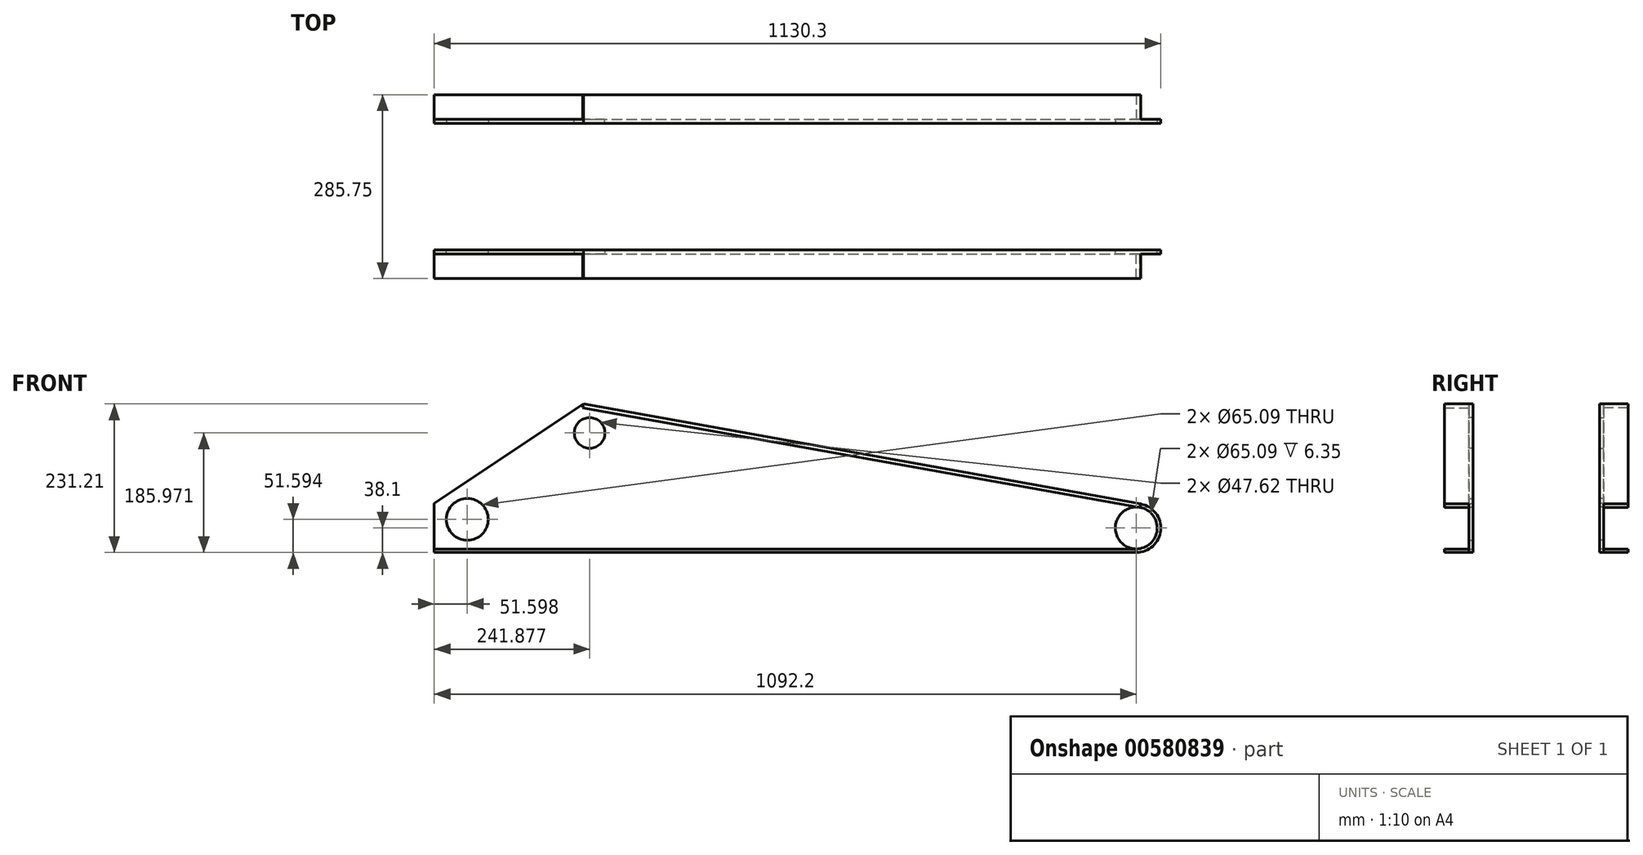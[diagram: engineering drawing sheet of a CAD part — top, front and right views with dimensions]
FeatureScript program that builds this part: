
annotation { "Feature Type Name" : "Feature", "Feature Type Description" : "" }
export const myFeature = defineFeature(function(context is Context, id is Id, definition is map)
    precondition{}
    {
        {
            var Q0;
            Q0=qCreatedBy(makeId("Front.planeOp"),FACE);
            var sketch = newSketch(context, id + "F0", { "sketchPlane" : qUnion([Q0])});
            skCircle(sketch, "E0", {"center": v(255.8, 0) * mm, "radius": 38.1 * mm});
            skLineSegment(sketch, "E1", {"start": v(-836.4, -38.1) * mm, "end": v(255.8, -38.1) * mm});
            skLineSegment(sketch, "E2", {"start": v(-836.4, -38.1) * mm, "end": v(-836.4, 38.1) * mm});
            skLineSegment(sketch, "E3", {"start": v(-836.4, 38.1) * mm, "end": v(-603.94, 193.11) * mm});
            skLineSegment(sketch, "E4", {"start": v(-603.94, 193.11) * mm, "end": v(262.54, 37.5) * mm});
            skCircle(sketch, "E5", {"center": v(-784.8, 13.5) * mm, "radius": 32.54 * mm});
            skCircle(sketch, "E6", {"center": v(255.8, 0) * mm, "radius": 32.54 * mm});
            skSolve(sketch);
        }
        {
            var Q0;
            {var subQ0=sQuery(id+"F0.wireOp",EDGE,"E1");Q0=makeQuery(id+"F0.imprint","IMPRINT",FACE,{"disambiguationData":[TD([[makeQuery(id+"F0.imprint","IMPRINT",EDGE,{"derivedFrom":subQ0}),1.0]])]});}
            var Q1;
            Q1=makeQuery(id+"F0.imprint","IMPRINT",FACE,{"disambiguationData":[TD([[makeQuery(id+"F0.imprint","IMPRINT",EDGE,{"derivedFrom":sQuery(id+"F0.wireOp",EDGE,"E6")}),-1.0]])]});
            var Q2;
            Q2=makeQuery(id+"F0.imprint","IMPRINT",FACE,{"disambiguationData":[TD([[makeQuery(id+"F0.imprint","IMPRINT",EDGE,{"derivedFrom":sQuery(id+"F0.wireOp",EDGE,"E2")}),-1.0]])]});
            var Q3;
            Q3=makeQuery(id+"F0.imprint","IMPRINT",FACE,{"disambiguationData":[TD([[makeQuery(id+"F0.imprint","IMPRINT",EDGE,{"derivedFrom":sQuery(id+"F0.wireOp",EDGE,"E4")}),1.0]])]});
            var Q4;
            Q4=makeQuery(id+"F0.imprint","IMPRINT",FACE,{"disambiguationData":[TD([[makeQuery(id+"F0.imprint","IMPRINT",EDGE,{"derivedFrom":sQuery(id+"F0.wireOp",EDGE,"E1")}),-1.0]])]});
            extrude(context, id + "F1", {"entities" : qUnion([Q0, Q1, Q2, Q3, Q4]), "depth" : 6.35 * mm, "offsetDistance" : 25.4 * mm});
        }
        {
            var Q0;
            {var subQ0=sQuery(id+"F0.wireOp",EDGE,"E2");var subQ1=sQuery(id+"F0.wireOp",EDGE,"E6");var subQ2=sQuery(id+"F0.wireOp",EDGE,"E5");var subQ3=sQuery(id+"F0.wireOp",EDGE,"E4");var subQ4=sQuery(id+"F0.wireOp",EDGE,"E3");var subQ5=makeQuery(id+"F1.opExtrude","CAP_FACE",FACE,{"disambiguationData":[OSD([sQuery(id+"F0.wireOp",EDGE,"E0"),sQuery(id+"F0.wireOp",EDGE,"E1"),subQ0,subQ4,subQ3,subQ2,subQ1])],"isStart":false});Q0=makeQuery(id+"FXa5xh8lsfBcW2b_1.boolean.opBoolean","SPLIT",FACE,{"disambiguationData":[TD([makeQuery(id+"F1.opExtrude","SWEPT_FACE",FACE,{"disambiguationData":[OSD([subQ0])]})])],"derivedFrom":subQ5});}
            var sketch = newSketch(context, id + "F2", { "sketchPlane" : qUnion([Q0])});
            skCircle(sketch, "E7", {"center": v(-594.52, 147.87) * mm, "radius": 23.81 * mm});
            skLineSegment(sketch, "E8", {"start": v(-603.94, 193.11) * mm, "end": v(262.54, 37.5) * mm});
            skLineSegment(sketch, "E9.bottom", {"start": v(-836.4, -38.1) * mm, "end": v(255.8, -38.1) * mm});
            skLineSegment(sketch, "E9.top", {"start": v(-836.4, -32.54) * mm, "end": v(255.8, -32.54) * mm});
            skLineSegment(sketch, "E9.left", {"start": v(-836.4, -38.1) * mm, "end": v(-836.4, -32.54) * mm});
            skLineSegment(sketch, "E9.right", {"start": v(255.8, -38.1) * mm, "end": v(255.8, -32.54) * mm});
            skLineSegment(sketch, "E10", {"start": v(-603.94, 193.11) * mm, "end": v(-605.06, 186.86) * mm});
            skLineSegment(sketch, "E11", {"start": v(-605.06, 186.86) * mm, "end": v(261.53, 32.04) * mm});
            skLineSegment(sketch, "E12", {"start": v(261.53, 32.04) * mm, "end": v(262.54, 37.5) * mm});
            skSolve(sketch);
        }
        {
            var Q0;
            Q0 = qSketchRegion(id + "F2", true);
            extrude(context, id + "F3", {"entities" : qUnion([Q0]), "operationType" : NewBodyOperationType.ADD, "depth" : 38.1 * mm, "offsetDistance" : 25.4 * mm});
        }
        {
            var Q0;
            Q0=makeQuery(id+"F2.imprint","IMPRINT",FACE,{"disambiguationData":[TD([[makeQuery(id+"F2.imprint","IMPRINT",EDGE,{"derivedFrom":sQuery(id+"F2.wireOp",EDGE,"E7")}),1.0]])]});
            extrude(context, id + "F4", {"entities" : qUnion([Q0]), "operationType" : NewBodyOperationType.REMOVE, "oppositeDirection" : true, "depth" : 25.4 * mm, "offsetDistance" : 25.4 * mm, "hasSecondDirection" : true, "secondDirectionOppositeDirection" : false, "secondDirectionDepth" : 76.2 * mm});
        }
        {
            var Q0;
            Q0=makeQuery(id+"F1.opExtrude","CAP_FACE",FACE,{"disambiguationData":[OSD([sQuery(id+"F0.wireOp",EDGE,"E0"),sQuery(id+"F0.wireOp",EDGE,"E1"),sQuery(id+"F0.wireOp",EDGE,"E2"),sQuery(id+"F0.wireOp",EDGE,"E3"),sQuery(id+"F0.wireOp",EDGE,"E4"),sQuery(id+"F0.wireOp",EDGE,"E5"),sQuery(id+"F0.wireOp",EDGE,"E6")])],"isStart":true});
            cPlane(context, id + "F5", {"entities" : qUnion([Q0]), "cplaneType" : CPlaneType.OFFSET, "offset" : 98.42 * mm, "width" : 152.4 * mm, "height" : 152.4 * mm});
        }
        {
            var Q0;
            Q0=makeQuery(id+"F1.opExtrude","SWEPT_BODY",BODY,{"disambiguationData":[OSD([sQuery(id+"F0.wireOp",EDGE,"E0"),sQuery(id+"F0.wireOp",EDGE,"E1"),sQuery(id+"F0.wireOp",EDGE,"E2"),sQuery(id+"F0.wireOp",EDGE,"E3"),sQuery(id+"F0.wireOp",EDGE,"E4"),sQuery(id+"F0.wireOp",EDGE,"E5"),sQuery(id+"F0.wireOp",EDGE,"E6")])]});
            var Q1;
            Q1=qCreatedBy(id+"F5.planeOp",FACE);
            mirror(context, id + "F6", {"entities" : qUnion([Q0]), "mirrorPlane" : qUnion([Q1])});
        }
    });
